# Revit family: LHBD-L05P77
name_source: partatom
category: Lighting Fixtures
units: mm (PartAtom-declared; Revit-internal decimal feet)

## family parameters
Always vertical = Yes
Cut with Voids When Loaded = No
Host = Ceiling
Light Source = Yes
OmniClass Number = 23.80.70.11.14.11
OmniClass Title = Downlights
Part Type = Normal
Room Calculation Point = No
Round Connector Dimension = Use Diameter
Shared = No

## types (4) — shared parameters
Assembly Code = D5020200
Color Filter = 16777215
Description = LED Pendant Mount High Bay D
Dimming Lamp Color Temperature Shift = <None>
Emit Shape Visible in Rendering = No
Emit from Rectangle Width = 0' - 9 13/16"
Height = 0' - 4 11/16"
Housing Finish = Metal - Viscor - White
Lamp = LED
Lens Finish = Acrylic - Viscor - Frosted, Impact Round Extruded
Louver Finish = Metal - Viscor - White Gloss F06
Manufacturer = VISIONEERING by VISCOR
Model = LHBD
Tilt Angle = 90.00°
URL = https://www.viscor.com
Voltage = 120 V
Width = 0' - 9 13/16"

## per-type parameters (varying)
| type | Apparent Load | Emit from Rectangle Length | Lamp Wattage | Length | Photometric Web File |
| LHBD48-LED840K080LUNV-L05P77 | 52 VA | 3' - 10 1/16" | 52 VA | 3' - 10 1/16" | LHBD48-LED840K080LUNV-L05P77-G001987.IES |
| LHBD48-LED840K120LUNV-L05P77 | 87 VA | 3' - 10 1/16" | 87 VA | 3' - 10 1/16" | LHBD48-LED840K120LUNV-L05P77-G001985.IES |
| LHBD96-LED840K160LUNV-L05P77 | 104 VA | 7' - 8 1/16" | 104 VA | 7' - 8 1/16" | LHBD96-LED840K160LUNV-L05P77.ies |
| LHBD96-LED840K240LUNV-L05P77 | 173 VA | 7' - 8 1/16" | 173 VA | 7' - 8 1/16" | LHBD96-LED840K240LUNV-L05P77.ies |

## geometry (parser evidence)
native form markers: Sweep x3
no freeform markers — native parametric forms only
